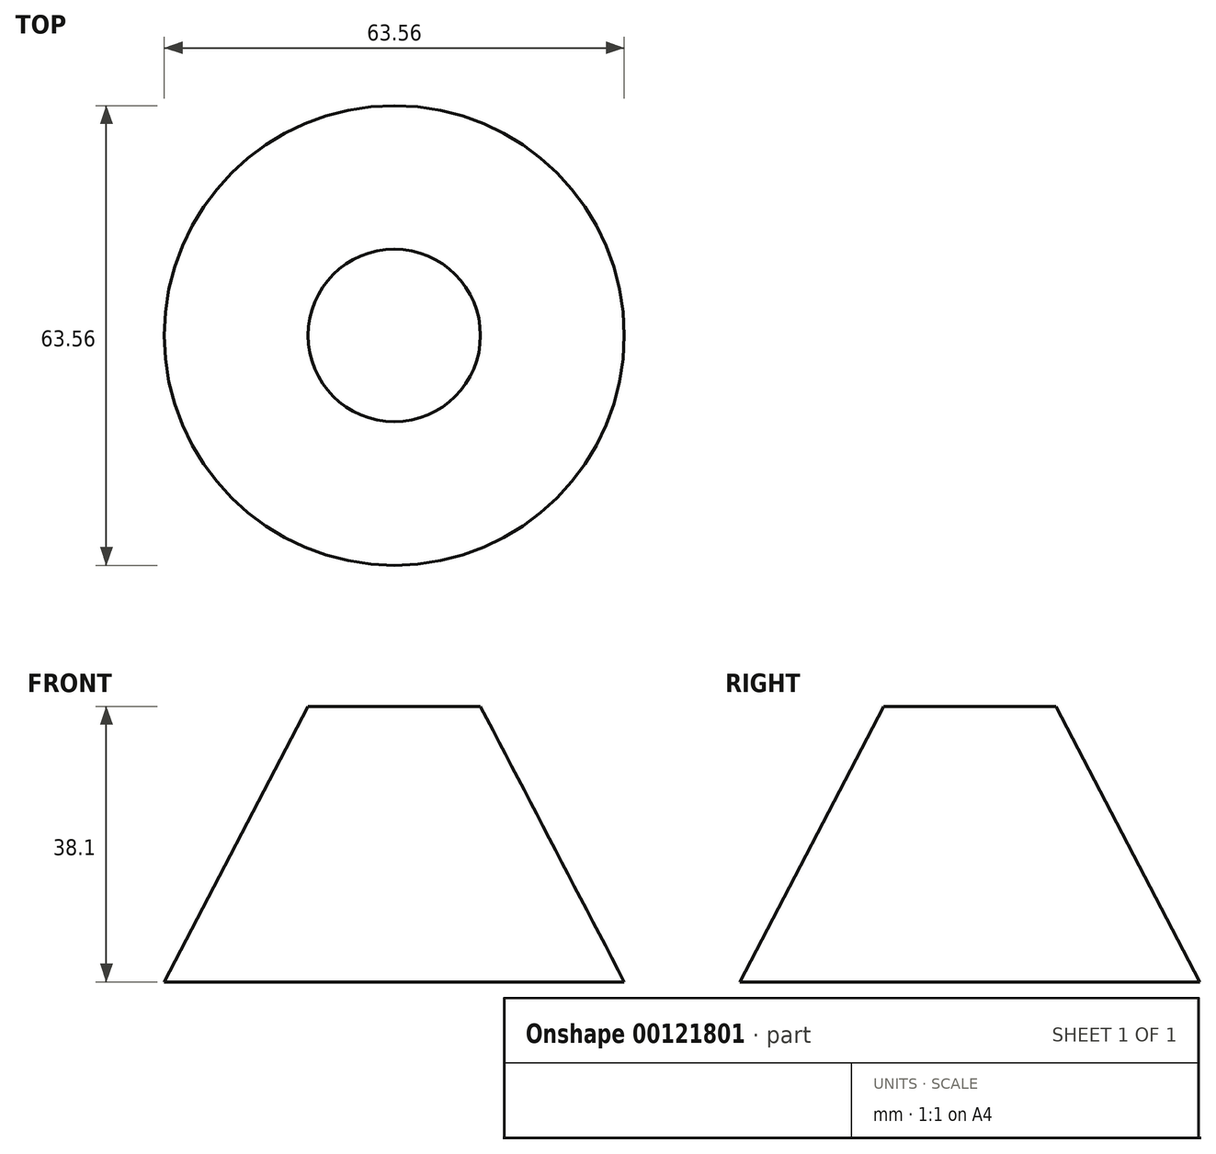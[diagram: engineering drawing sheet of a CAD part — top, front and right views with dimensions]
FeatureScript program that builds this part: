
annotation { "Feature Type Name" : "Feature", "Feature Type Description" : "" }
export const myFeature = defineFeature(function(context is Context, id is Id, definition is map)
    precondition{}
    {
        {
            var Q0;
            Q0=qCreatedBy(makeId("Top.planeOp"),FACE);
            var sketch = newSketch(context, id + "F0", { "sketchPlane" : qUnion([Q0])});
            skCircle(sketch, "E0", {"center": v(0, 0) * mm, "radius": 31.78 * mm});
            skSolve(sketch);
        }
        {
            var Q0;
            Q0=qCreatedBy(makeId("Top.planeOp"),FACE);
            cPlane(context, id + "F1", {"entities" : qUnion([Q0]), "cplaneType" : CPlaneType.OFFSET, "offset" : 38.1 * mm, "width" : 152.4 * mm, "height" : 152.4 * mm});
        }
        {
            var Q0;
            Q0=qCreatedBy(id+"F1.planeOp",FACE);
            var sketch = newSketch(context, id + "F2", { "sketchPlane" : qUnion([Q0])});
            skCircle(sketch, "E1", {"center": v(0, 0) * mm, "radius": 11.91 * mm});
            skSolve(sketch);
        }
        {
            var Q0;
            Q0=makeQuery(id+"F0.imprint","IMPRINT",FACE,{"disambiguationData":[TD([[makeQuery(id+"F0.imprint","IMPRINT",EDGE,{"derivedFrom":sQuery(id+"F0.wireOp",EDGE,"E0")}),1.0]])]});
            var Q1;
            Q1=makeQuery(id+"F2.imprint","IMPRINT",FACE,{"disambiguationData":[TD([[makeQuery(id+"F2.imprint","IMPRINT",EDGE,{"derivedFrom":sQuery(id+"F2.wireOp",EDGE,"E1")}),1.0]])]});
            loft(context, id + "F3", {"sheetProfilesArray" : [{ "sheetProfileEntities" : qUnion([Q0]) }, { "sheetProfileEntities" : qUnion([Q1]) }]});
        }
    });
